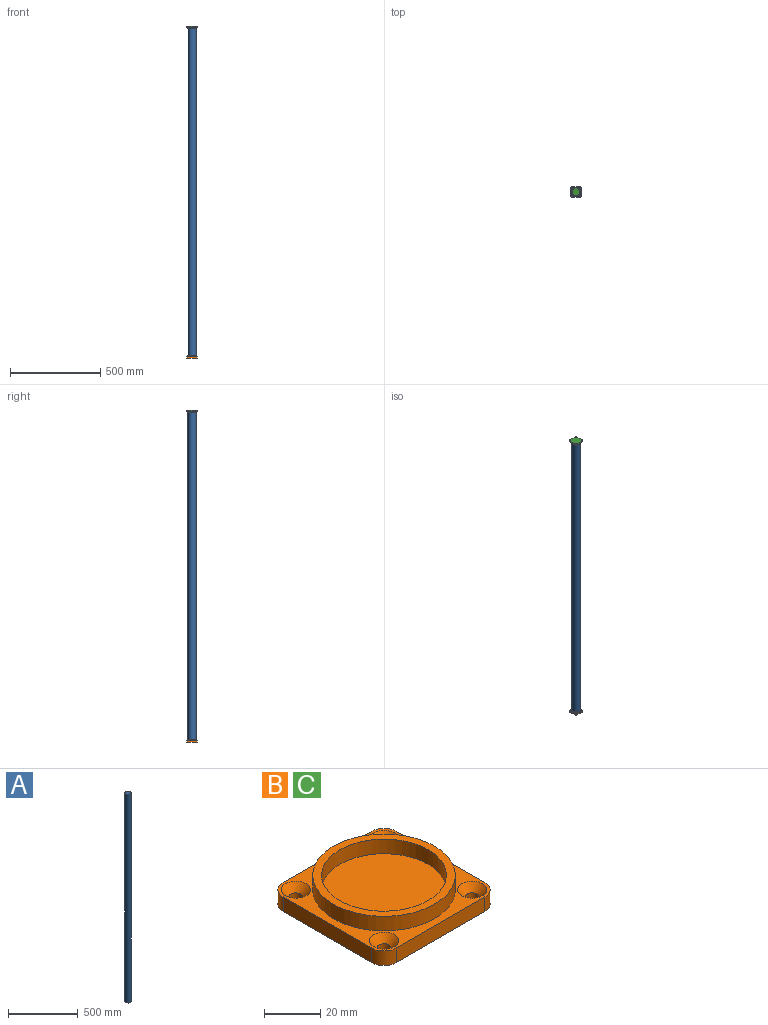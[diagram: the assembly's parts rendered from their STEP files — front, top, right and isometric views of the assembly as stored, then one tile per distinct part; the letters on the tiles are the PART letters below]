
ASSEMBLY  parts=3 mates=3
PART A: 3 faces, bbox 44.5x44.5x1828.8 mm
  f0: cylinder r=22.23mm len=1828.8mm, axis (0,0,-1), area 255380.6mm2, adj f1,f2
  f1: plane 44.45x44.45mm, normal (0,0,1), area 1551.8mm2, adj f0
  f2: plane 44.45x44.45mm, normal (0,0,-1), area 1551.8mm2, adj f0
PART B: 22 faces, bbox 57.2x57.2x12.7 mm
  f0: plane 44.45x6.35mm, normal (1,0,0), area 282.3mm2, adj f4,f5,f18,f21
  f1: plane 44.45x6.35mm, normal (0,1,0), area 282.3mm2, adj f4,f5,f18,f19
  f2: plane 44.45x6.35mm, normal (-1,0,0), area 282.3mm2, adj f4,f5,f19,f20
  f3: plane 44.45x6.35mm, normal (0,-1,0), area 282.3mm2, adj f4,f5,f20,f21
  f4: plane 57.15x57.15mm, normal (0,0,1), area 862.3mm2, adj f0,f1,f2,f3,f7,f9,f11,f13
  f5: plane 57.15x57.15mm, normal (0,0,-1), area 3153.6mm2, adj f0,f1,f2,f3,f6,f8,f10,f12
  f6: cylinder r=2.49mm len=4.98mm, axis (0,0,1), area 50.2mm2, adj f5,f7
  f7: cone r=2.49mm half-angle=41deg, axis (0,0,1), area 100.8mm2, adj f4,f6
  f8: cylinder r=2.49mm len=4.98mm, axis (0,0,1), area 50.2mm2, adj f5,f9
  f9: cone r=2.49mm half-angle=41deg, axis (0,0,1), area 100.8mm2, adj f4,f8
  f10: cylinder r=2.49mm len=4.98mm, axis (0,0,1), area 50.2mm2, adj f5,f11
  f11: cone r=2.49mm half-angle=41deg, axis (0,0,1), area 100.8mm2, adj f4,f10
  f12: cylinder r=2.49mm len=4.98mm, axis (0,0,1), area 50.2mm2, adj f5,f13
  f13: cone r=2.49mm half-angle=41deg, axis (0,0,1), area 100.8mm2, adj f4,f12
  f14: cylinder r=22.23mm len=44.45mm, axis (0,0,-1), area 886.7mm2, adj f16,f17
  f15: cylinder r=25.4mm len=50.8mm, axis (0,0,-1), area 1013.4mm2, adj f4,f16
  f16: plane 50.8x50.8mm, normal (0,0,1), area 475mm2, adj f14,f15
  f17: plane 44.45x44.45mm, normal (0,0,1), area 1551.8mm2, adj f14
  f18: cylinder r=6.35mm len=6.35mm, axis (0,0,-1), area 63.3mm2, adj f0,f1,f4,f5
  f19: cylinder r=6.35mm len=6.35mm, axis (0,0,1), area 63.3mm2, adj f1,f2,f4,f5
  f20: cylinder r=6.35mm len=6.35mm, axis (0,0,-1), area 63.3mm2, adj f2,f3,f4,f5
  f21: cylinder r=6.35mm len=6.35mm, axis (0,0,1), area 63.3mm2, adj f0,f3,f4,f5
PART C: same geometry as B
PLACE A t=(-89.07,-158.59,-146.85)mm fixed
PLACE B t=(-89.07,-158.59,-153.2)mm
PLACE C rot(axis=(0,1,0),180deg) t=(-89.07,-158.59,1688.3)mm
MATE planar C.f2 <-> B.f0  axis (1,0,0) through (-60.5,-158.59,1685.13)mm
MATE fastened C.f14 <-> A.f0  axis (0,0,-1) through (-89.07,-158.59,1681.95)mm
MATE fastened B.f14 <-> A.f0  axis (0,0,1) through (-89.07,-158.59,-146.85)mm
